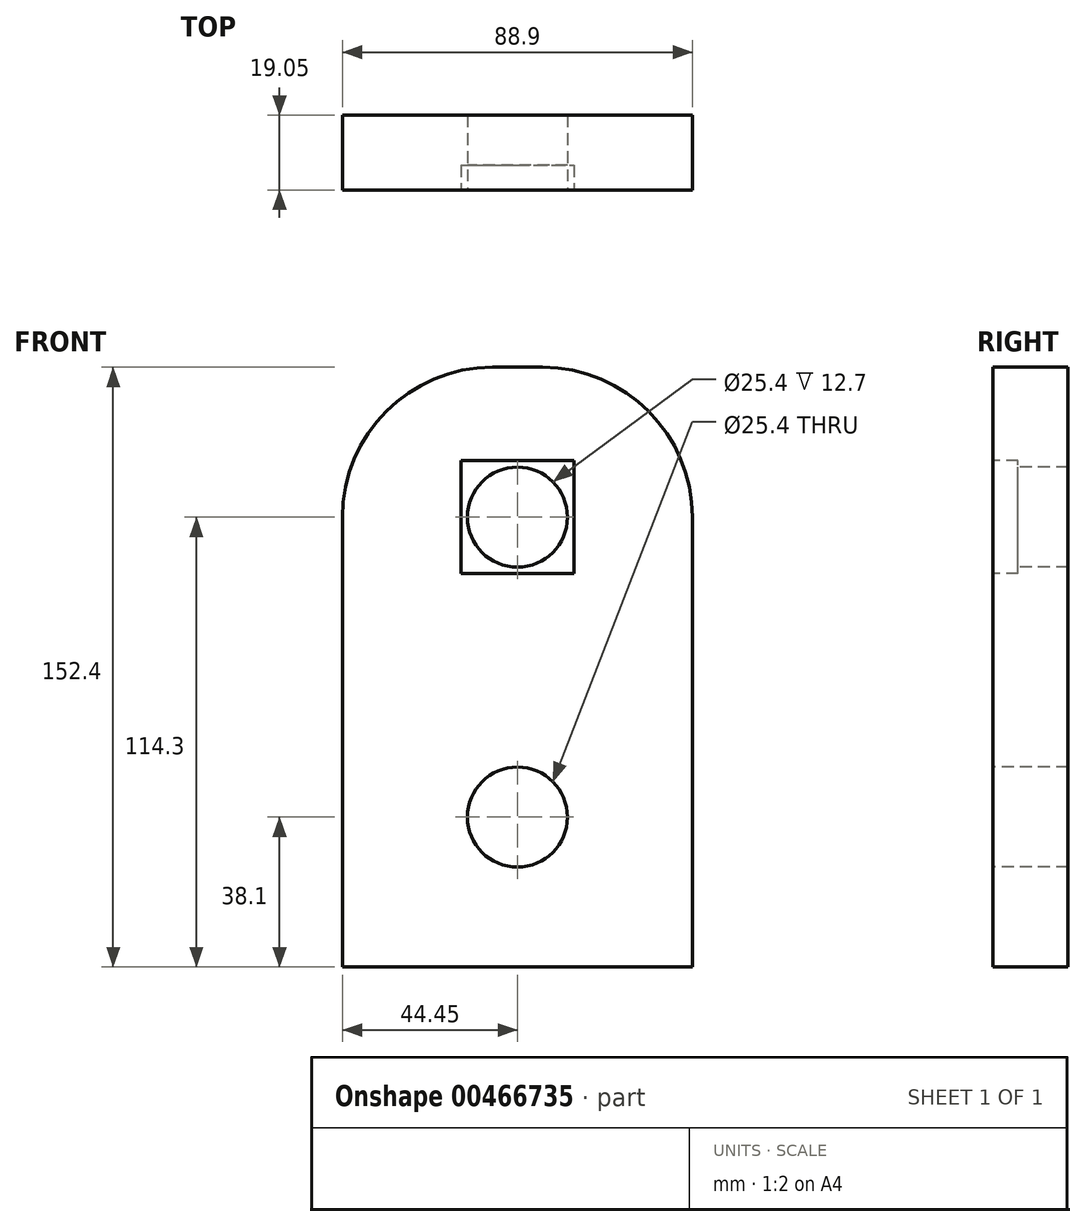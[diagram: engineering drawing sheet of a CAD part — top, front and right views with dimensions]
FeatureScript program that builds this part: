
annotation { "Feature Type Name" : "Feature", "Feature Type Description" : "" }
export const myFeature = defineFeature(function(context is Context, id is Id, definition is map)
    precondition{}
    {
        {
            var Q0;
            Q0=qCreatedBy(makeId("Front.planeOp"),FACE);
            var sketch = newSketch(context, id + "F0", { "sketchPlane" : qUnion([Q0])});
            skLineSegment(sketch, "E0.bottom", {"start": v(-44.45, -76.2) * mm, "end": v(44.45, -76.2) * mm});
            skLineSegment(sketch, "E0.top", {"start": v(-6.35, 76.2) * mm, "end": v(6.35, 76.2) * mm});
            skLineSegment(sketch, "E0.left", {"start": v(-44.45, -76.2) * mm, "end": v(-44.45, 38.1) * mm});
            skLineSegment(sketch, "E0.right", {"start": v(44.45, -76.2) * mm, "end": v(44.45, 38.1) * mm});
            skPoint(sketch, "E0.middle", {"position": v(0, 0) * mm});
            skPoint(sketch, "E1.visualSharp", {"position": v(-44.45, 76.2) * mm});
            skArc(sketch, "E1.filletArc", {"start": v(-6.35, 76.2) * mm, "mid": v(-33.3, 65.04) * mm, "end": v(-44.45, 38.1) * mm});
            skPoint(sketch, "E2.visualSharp", {"position": v(44.45, 76.2) * mm});
            skArc(sketch, "E2.filletArc", {"start": v(44.45, 38.1) * mm, "mid": v(33.3, 65.04) * mm, "end": v(6.35, 76.2) * mm});
            skSolve(sketch);
        }
        {
            var Q0;
            Q0 = qSketchRegion(id + "F0", true);
            extrude(context, id + "F1", {"entities" : qUnion([Q0]), "depth" : 19.05 * mm});
        }
        {
            var Q0;
            Q0=makeQuery(id+"F1.opExtrude","CAP_FACE",FACE,{"disambiguationData":[OSD([sQuery(id+"F0.wireOp",EDGE,"E0.bottom"),sQuery(id+"F0.wireOp",EDGE,"E0.top"),sQuery(id+"F0.wireOp",EDGE,"E0.left"),sQuery(id+"F0.wireOp",EDGE,"E0.right"),sQuery(id+"F0.wireOp",EDGE,"E1.filletArc"),sQuery(id+"F0.wireOp",EDGE,"E2.filletArc")])],"isStart":false});
            var sketch = newSketch(context, id + "F2", { "sketchPlane" : qUnion([Q0])});
            skCircle(sketch, "E3", {"center": v(0, -38.1) * mm, "radius": 12.7 * mm});
            skCircle(sketch, "E4", {"center": v(0, 38.1) * mm, "radius": 12.7 * mm});
            skSolve(sketch);
        }
        {
            var Q0;
            Q0 = qSketchRegion(id + "F2", true);
            extrude(context, id + "F3", {"entities" : qUnion([Q0]), "operationType" : NewBodyOperationType.REMOVE, "endBound" : BoundingType.THROUGH_ALL, "oppositeDirection" : true, "depth" : 25.4 * mm});
        }
        {
            var Q0;
            Q0=makeQuery(id+"F1.opExtrude","CAP_FACE",FACE,{"disambiguationData":[OSD([sQuery(id+"F0.wireOp",EDGE,"E0.bottom"),sQuery(id+"F0.wireOp",EDGE,"E0.top"),sQuery(id+"F0.wireOp",EDGE,"E0.left"),sQuery(id+"F0.wireOp",EDGE,"E0.right"),sQuery(id+"F0.wireOp",EDGE,"E1.filletArc"),sQuery(id+"F0.wireOp",EDGE,"E2.filletArc")])],"isStart":false});
            var sketch = newSketch(context, id + "F4", { "sketchPlane" : qUnion([Q0])});
            skLineSegment(sketch, "E5.bottom", {"start": v(14.35, -52.45) * mm, "end": v(-14.35, -52.45) * mm});
            skLineSegment(sketch, "E5.top", {"start": v(14.35, -23.75) * mm, "end": v(-14.35, -23.75) * mm});
            skLineSegment(sketch, "E5.left", {"start": v(14.35, -52.45) * mm, "end": v(14.35, -23.75) * mm});
            skLineSegment(sketch, "E5.right", {"start": v(-14.35, -52.45) * mm, "end": v(-14.35, -23.75) * mm});
            skPoint(sketch, "E5.middle", {"position": v(0, -38.1) * mm});
            skLineSegment(sketch, "E6.bottom", {"start": v(-14.35, 23.75) * mm, "end": v(14.35, 23.75) * mm});
            skLineSegment(sketch, "E6.top", {"start": v(-14.35, 52.45) * mm, "end": v(14.35, 52.45) * mm});
            skLineSegment(sketch, "E6.left", {"start": v(-14.35, 23.75) * mm, "end": v(-14.35, 52.45) * mm});
            skLineSegment(sketch, "E6.right", {"start": v(14.35, 23.75) * mm, "end": v(14.35, 52.45) * mm});
            skPoint(sketch, "E6.middle", {"position": v(0, 38.1) * mm});
            skSolve(sketch);
        }
        {
            var Q0;
            Q0=makeQuery(id+"F4.imprint","IMPRINT",FACE,{"disambiguationData":[TD([[makeQuery(id+"F4.imprint","IMPRINT",EDGE,{"derivedFrom":sQuery(id+"F4.wireOp",EDGE,"E6.bottom")}),1.0]])]});
            extrude(context, id + "F5", {"entities" : qUnion([Q0]), "operationType" : NewBodyOperationType.REMOVE, "oppositeDirection" : true, "depth" : 6.35 * mm});
        }
    });
